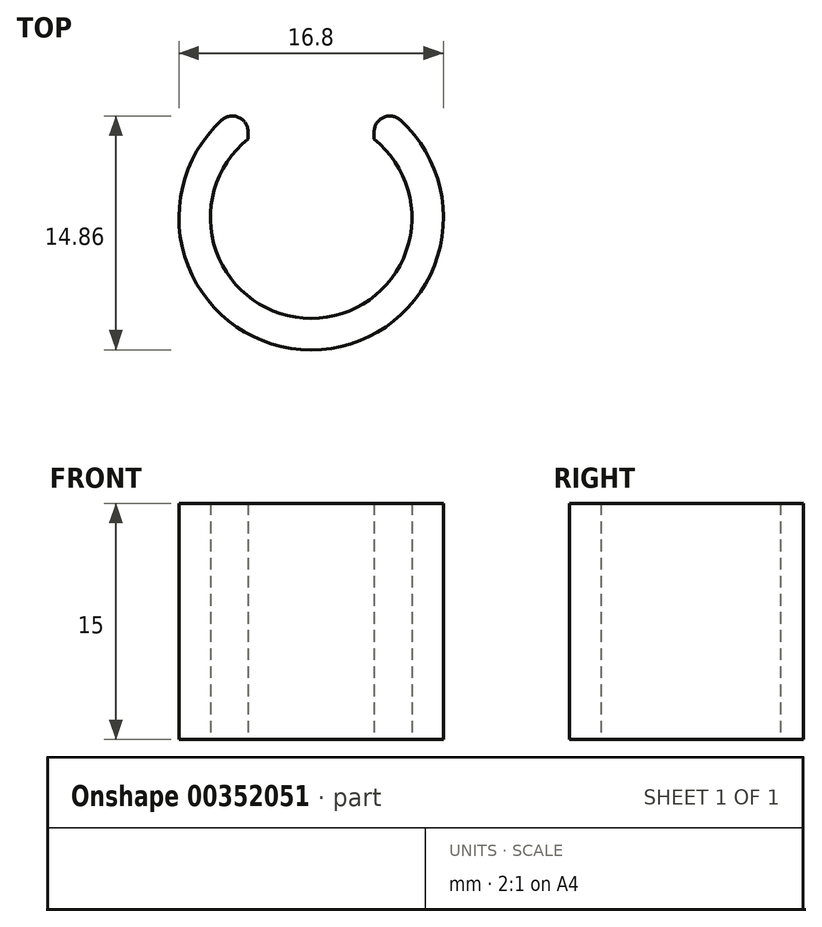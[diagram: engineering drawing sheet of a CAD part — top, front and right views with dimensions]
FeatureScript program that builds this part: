
annotation { "Feature Type Name" : "Feature", "Feature Type Description" : "" }
export const myFeature = defineFeature(function(context is Context, id is Id, definition is map)
    precondition{}
    {
        {
            var Q0;
            Q0=qCreatedBy(makeId("Top.planeOp"),FACE);
            var sketch = newSketch(context, id + "F0", { "sketchPlane" : qUnion([Q0])});
            skLineSegment(sketch, "E0.left", {"start": v(4, 5) * mm, "end": v(4, 5.46) * mm});
            skLineSegment(sketch, "E0.right", {"start": v(-4, 5) * mm, "end": v(-4, 5.46) * mm});
            skArc(sketch, "E1", {"start": v(-4, 5) * mm, "mid": v(0, -6.4) * mm, "end": v(4, 5) * mm});
            skArc(sketch, "E2", {"start": v(-5.68, 6.2) * mm, "mid": v(0, -8.4) * mm, "end": v(5.68, 6.2) * mm});
            skPoint(sketch, "E3.visualSharp", {"position": v(-4, 7.39) * mm});
            skArc(sketch, "E3.filletArc", {"start": v(-4, 5.46) * mm, "mid": v(-4.6, 6.37) * mm, "end": v(-5.68, 6.2) * mm});
            skPoint(sketch, "E4.visualSharp", {"position": v(4, 7.39) * mm});
            skArc(sketch, "E4.filletArc", {"start": v(5.68, 6.2) * mm, "mid": v(4.6, 6.37) * mm, "end": v(4, 5.46) * mm});
            skSolve(sketch);
        }
        {
            var Q0;
            Q0=makeQuery(id+"F0.imprint","IMPRINT",FACE,{"disambiguationData":[TD([[makeQuery(id+"F0.imprint","IMPRINT",EDGE,{"derivedFrom":sQuery(id+"F0.wireOp",EDGE,"E0.left")}),-1.0]])]});
            extrude(context, id + "F1", {"entities" : qUnion([Q0]), "depth" : 15 * mm});
        }
    });
